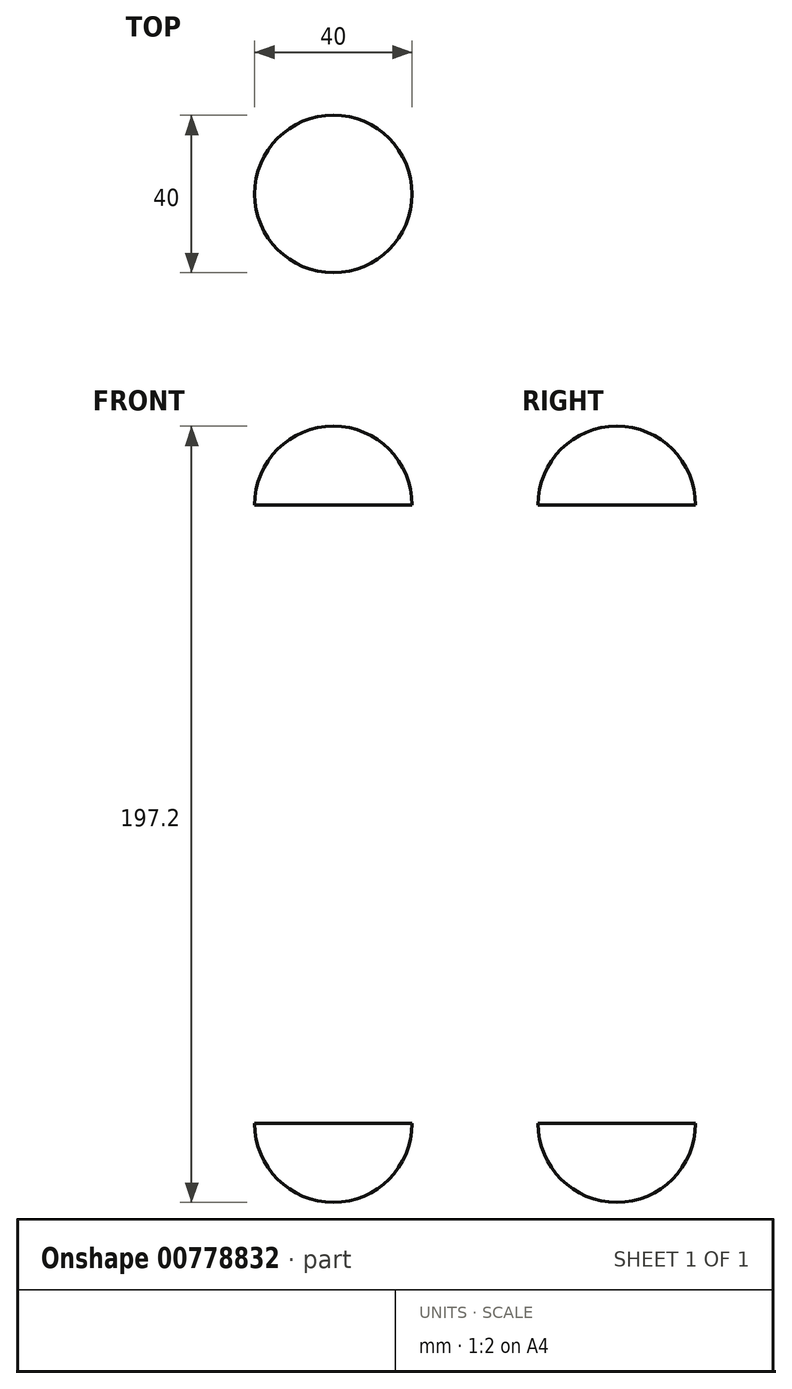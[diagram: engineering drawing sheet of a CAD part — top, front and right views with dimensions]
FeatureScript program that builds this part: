
annotation { "Feature Type Name" : "Feature", "Feature Type Description" : "" }
export const myFeature = defineFeature(function(context is Context, id is Id, definition is map)
    precondition{}
    {
        {
            var Q0;
            Q0=qCreatedBy(makeId("Front.planeOp"),FACE);
            var sketch = newSketch(context, id + "F0", { "sketchPlane" : qUnion([Q0])});
            skArc(sketch, "E0", {"start": v(20, 0) * mm, "mid": v(0, 20) * mm, "end": v(-20, 0) * mm});
            skLineSegment(sketch, "E1", {"start": v(-20, 0) * mm, "end": v(20, 0) * mm});
            skSolve(sketch);
        }
        {
            var Q0;
            Q0=makeQuery(id+"F0.imprint","IMPRINT",FACE,{"disambiguationData":[TD([[makeQuery(id+"F0.imprint","IMPRINT",EDGE,{"derivedFrom":sQuery(id+"F0.wireOp",EDGE,"E0")}),1.0]])]});
            var Q1;
            Q1=sQuery(id+"F0.wireOp",EDGE,"E1");
            revolve(context, id + "F1", {"surfaceOperationType" : NewSurfaceOperationType.NEW, "entities" : qUnion([Q0]), "axis" : qUnion([Q1]), "revolveType" : RevolveType.SYMMETRIC, "angle" : 180 * degree});
        }
        {
            var Q0;
            Q0=makeQuery(id+"F1.opRevolve","SWEPT_BODY",BODY,{"disambiguationData":[OSD([sQuery(id+"F0.wireOp",EDGE,"E0"),sQuery(id+"F0.wireOp",EDGE,"E1")])]});
            transform(context, id + "F2", {"entities" : qUnion([Q0]), "transformType" : TransformType.TRANSLATION_3D, "dx" : 0 * mm, "dy" : 0 * mm, "dz" : 78.6 * mm, "makeCopy" : false});
        }
        {
            var Q0;
            Q0=makeQuery(id+"F1.opRevolve","SWEPT_BODY",BODY,{"disambiguationData":[OSD([sQuery(id+"F0.wireOp",EDGE,"E0"),sQuery(id+"F0.wireOp",EDGE,"E1")])]});
            var Q1;
            Q1=qCreatedBy(makeId("Top.planeOp"),FACE);
            mirror(context, id + "F3", {"entities" : qUnion([Q0]), "mirrorPlane" : qUnion([Q1])});
        }
    });
